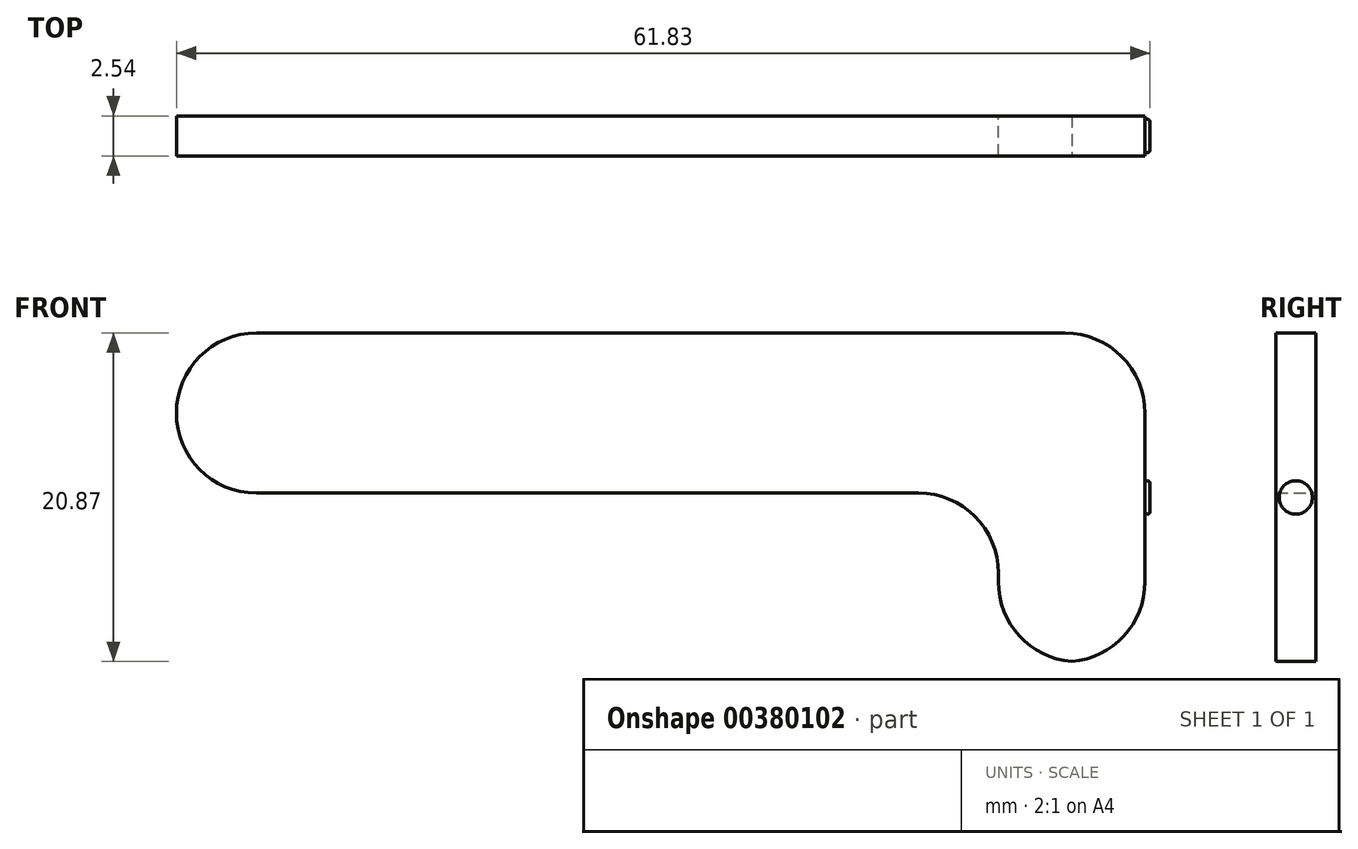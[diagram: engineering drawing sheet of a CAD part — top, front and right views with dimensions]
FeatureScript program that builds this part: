
annotation { "Feature Type Name" : "Feature", "Feature Type Description" : "" }
export const myFeature = defineFeature(function(context is Context, id is Id, definition is map)
    precondition{}
    {
        {
            var Q0;
            Q0=qCreatedBy(makeId("Front.planeOp"),FACE);
            var sketch = newSketch(context, id + "F0", { "sketchPlane" : qUnion([Q0])});
            skLineSegment(sketch, "E0", {"start": v(-46.59, 28.49) * mm, "end": v(5.62, 28.49) * mm});
            skLineSegment(sketch, "E1", {"start": v(5.62, 28.49) * mm, "end": v(5.62, 17.76) * mm});
            skLineSegment(sketch, "E2", {"start": v(-46.59, 38.65) * mm, "end": v(14.93, 38.65) * mm});
            skLineSegment(sketch, "E3", {"start": v(14.93, 38.65) * mm, "end": v(14.93, 17.76) * mm});
            skLineSegment(sketch, "E4", {"start": v(5.62, 17.76) * mm, "end": v(14.93, 17.76) * mm});
            skLineSegment(sketch, "E5", {"start": v(-46.59, 38.65) * mm, "end": v(-46.59, 28.49) * mm});
            skSolve(sketch);
        }
        {
            var Q0;
            Q0 = qSketchRegion(id + "F0", true);
            extrude(context, id + "F1", {"entities" : qUnion([Q0]), "endBound" : BoundingType.SYMMETRIC, "depth" : 2.54 * mm});
        }
        {
            var Q0;
            Q0=makeQuery(id+"F1.opExtrude","SWEPT_EDGE",EDGE,{"disambiguationData":[OSD([sQuery(id+"F0.wireOp",EDGE,"E2"),sQuery(id+"F0.wireOp",EDGE,"E3")])]});
            var Q1;
            Q1=makeQuery(id+"F1.opExtrude","SWEPT_EDGE",EDGE,{"disambiguationData":[OSD([sQuery(id+"F0.wireOp",EDGE,"E3"),sQuery(id+"F0.wireOp",EDGE,"E4")])]});
            var Q2;
            Q2=makeQuery(id+"F1.opExtrude","SWEPT_EDGE",EDGE,{"disambiguationData":[OSD([sQuery(id+"F0.wireOp",EDGE,"E1"),sQuery(id+"F0.wireOp",EDGE,"E4")])]});
            var Q3;
            Q3=makeQuery(id+"F1.opExtrude","SWEPT_EDGE",EDGE,{"disambiguationData":[OSD([sQuery(id+"F0.wireOp",EDGE,"E0"),sQuery(id+"F0.wireOp",EDGE,"E1")])]});
            fillet(context, id + "F2", {"entities" : qUnion([Q0, Q1, Q2, Q3]), "radius" : 5.08 * mm, "tangentPropagation" : true, "allowEdgeOverflow" : false});
        }
        {
            var Q0;
            Q0=makeQuery(id+"F1.opExtrude","SWEPT_EDGE",EDGE,{"disambiguationData":[OSD([sQuery(id+"F0.wireOp",EDGE,"E2"),sQuery(id+"F0.wireOp",EDGE,"E5")])]});
            var Q1;
            Q1=makeQuery(id+"F1.opExtrude","SWEPT_EDGE",EDGE,{"disambiguationData":[OSD([sQuery(id+"F0.wireOp",EDGE,"E0"),sQuery(id+"F0.wireOp",EDGE,"E5")])]});
            fillet(context, id + "F3", {"entities" : qUnion([Q0, Q1]), "radius" : 5.08 * mm, "tangentPropagation" : true, "allowEdgeOverflow" : false});
        }
        {
            var Q0;
            Q0=makeQuery(id+"F1.opExtrude","SWEPT_FACE",FACE,{"disambiguationData":[OSD([sQuery(id+"F0.wireOp",EDGE,"E3")])]});
            var sketch = newSketch(context, id + "F4", { "sketchPlane" : qUnion([Q0])});
            skCircle(sketch, "E6", {"center": v(0, 28.2) * mm, "radius": 1.06 * mm});
            skPoint(sketch, "E6.centerSnap0", {"position": v(-1.27, 28.2) * mm});
            skPoint(sketch, "E6.centerSnap1", {"position": v(0, 22.84) * mm});
            skSolve(sketch);
        }
        {
            var Q0;
            Q0 = qSketchRegion(id + "F4", true);
            extrude(context, id + "F5", {"entities" : qUnion([Q0]), "depth" : 0.3 * mm});
        }
        {
            var Q0;
            Q0=makeQuery(id+"F5.opExtrude","CAP_EDGE",EDGE,{"disambiguationData":[OSD([sQuery(id+"F4.wireOp",EDGE,"E6")])],"isStart":false});
            fillet(context, id + "F6", {"entities" : qUnion([Q0]), "radius" : 0.13 * mm, "tangentPropagation" : true, "allowEdgeOverflow" : false});
        }
    });
